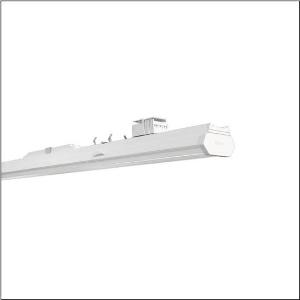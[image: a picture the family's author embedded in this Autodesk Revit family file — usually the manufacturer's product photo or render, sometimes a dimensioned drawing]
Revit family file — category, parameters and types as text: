
# Revit family: licross_r__11_protected_mo_51td12dn495g3s_4e23
name_source: partatom
category: Lighting Fixtures
units: mm (PartAtom-declared; Revit-internal decimal feet)

## family parameters
Cut with Voids When Loaded = No
Host = Face
Light Source = No
Part Type = Normal
Room Calculation Point = No
Round Connector Dimension = Use Diameter
Shared = No

## types (1)
- --- (1 x LED, 980 lm, 6.8 W, 4000K)
    Apparent Load = 7 VA
    CIE Flux Codes = 73 92 98 99 100
    Color Rendering = 80
    Color Temperature = 4000K
    Default Elevation = 1800 mm
    Description = Licross® 11 Protected MO, luminaire insert, of sheet steel, galvanised, coil coated, white, length: 1.500mm, width: 90mm, height: 101mm, LED rated luminous flux: 9.980lm, light colour: 840, control gear: DALI 2, with plug, 6-pole, with phase selection, for trunking rail, 14-core, mains connection: 220..240V, AC, 50/60Hz, rated input power: 61W, for trunking rail, 14-core, halogen-free wiring, for emergency light function, converter,control gear: single battery element, battery: LiFeP04, 9Ah, primary light control with lens, of plastic, primary optical cover: cover, of PMMA, light emission: direct distribution, primary light characteristic: symmetric, protection rating (complete): IP54, insulation class (complete): insulation class I (protective earthing), certification: CE, UKCA, protection symbol: D if used in an environment with non-conductive dust loads with corresponding accessories, impact resistance: IK06, permissible ambient temperature for indoor applications: +5..+35°C, standard: EN 60598-2-22, LABS conformity tested according to VDMA 24364:2018-05, reducing of maximum allowable ambient temperature of 5°C with ceiling mounting, corresponds to IFS (International Featured Standards) requirements for safety and quality in the food industry, packaging unit: 1 piece
    Height = 92 mm
    Lamp = 1 x LED
    Lamp Light Flux = 980 lm
    Lamp Power = 6.8 W
    Lamp count = 1
    Length = 1500 mm
    Luminous efficacy = 144 lm/W
    Manufacturer = Siteco
    ModVariant = No
    Model = 51TD12DN495G3S
    Mounting Place = Ceiling
    Mounting Type = Pendant
    Number of Poles = 1
    OnlyDefault = Yes
    Power Factor = 1
    Product Name = Licross® 11 Protected MO
    Product group = luminaire insert
    ProductGroupID = 901
    Protection Class = Protection class I
    Protection Degree = IP 54
    RLX_Detail_Level = 1
    RLX_Emergency_Light_Flux = 0 lm
    RLX_Emergency_Type = 0
    RLX_Emergency_Type_DB = No
    RlxData = <blob elided: 24725 chars, md5=aebf3ac6>
    Socket = socket
    Standby Power = 0 W
    System Light Flux = 980 lm
    System Power = 7 W
    Type Comments = : emergency light operation: 3 h
    Type Image = l_1256145.jpg
    URL = http://relux.com
    VarID = @adj_041305
    Voltage = 0 V
    Weight = 0.00 kg
    Width = 88 mm

## geometry (parser evidence)
native form markers: Blend x4, Sweep x10
no freeform markers — native parametric forms only
